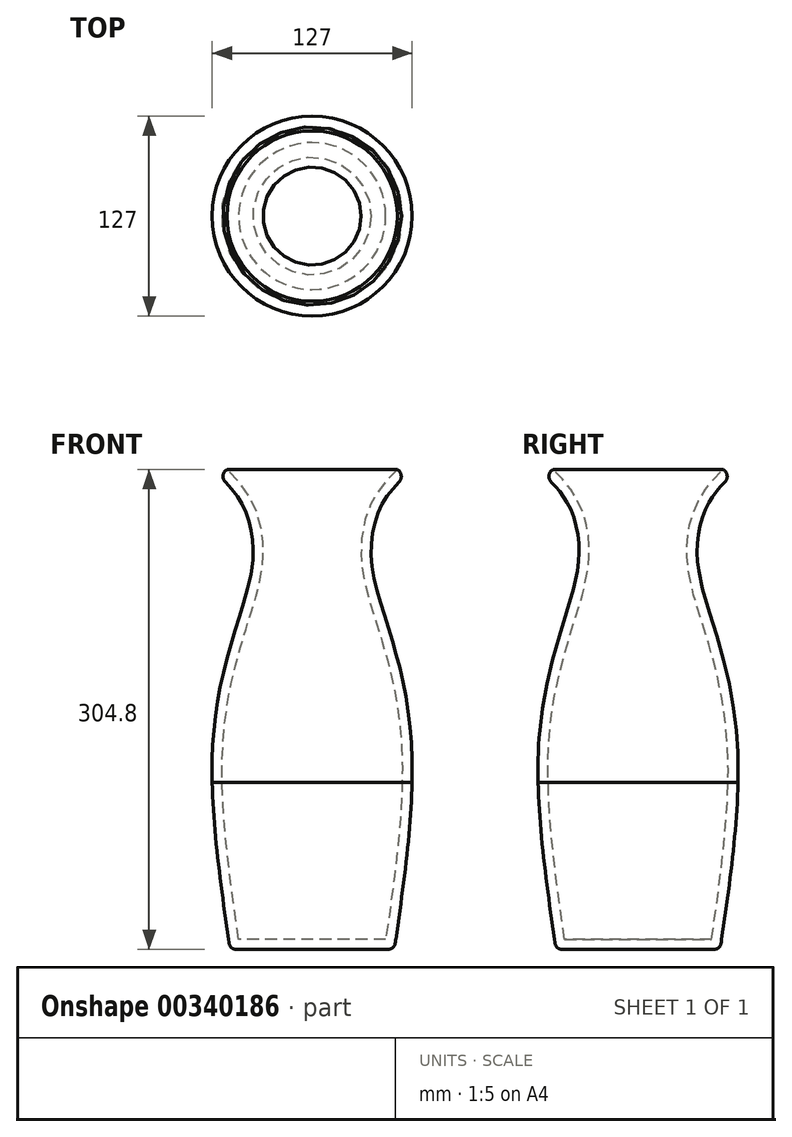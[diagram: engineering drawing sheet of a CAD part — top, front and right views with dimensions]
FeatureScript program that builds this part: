
annotation { "Feature Type Name" : "Feature", "Feature Type Description" : "" }
export const myFeature = defineFeature(function(context is Context, id is Id, definition is map)
    precondition{}
    {
        {
            var Q0;
            Q0=qCreatedBy(makeId("Front.planeOp"),FACE);
            var sketch = newSketch(context, id + "F0", { "sketchPlane" : qUnion([Q0])});
            skLineSegment(sketch, "E0.bottom", {"start": v(31.75, 152.4) * mm, "end": v(-31.75, 152.4) * mm});
            skLineSegment(sketch, "E0.top", {"start": v(31.75, -152.4) * mm, "end": v(-31.75, -152.4) * mm});
            skLineSegment(sketch, "E0.left", {"start": v(31.75, 152.4) * mm, "end": v(31.75, -152.4) * mm});
            skLineSegment(sketch, "E0.right", {"start": v(-31.75, 152.4) * mm, "end": v(-31.75, -152.4) * mm});
            skPoint(sketch, "E0.middle", {"position": v(0, 0) * mm});
            skFitSpline(sketch, "E1", {"points": [v(-31.75, 152.4) * mm, v(-13.17, 131.2) * mm, v(-5.9, 95.37) * mm, v(-19.4, 42.9) * mm, v(-31.75, -31.89) * mm, v(-20.44, -152.4) * mm], "startDerivative": vector(149.57, -137.06) * mm, "endDerivative": vector(63.8, -443.79) * mm});
            skFitSpline(sketch, "E2.0", {"points": [v(-27.46, 157.08) * mm, v(-25.9, 155.65) * mm, v(-22.73, 152.75) * mm, v(-17.97, 148.09) * mm, v(-14.14, 143.8) * mm, v(-11.26, 140.04) * mm, v(-9.55, 137.54) * mm, v(-8.26, 135.43) * mm, v(-7.02, 133.26) * mm, v(-5.6, 130.44) * mm, v(-4.09, 126.9) * mm, v(-2.34, 121.98) * mm, v(-0.66, 115.53) * mm, v(0.31, 108.73) * mm, v(0.64, 103.13) * mm, v(0.66, 99.58) * mm, v(0.56, 96.7) * mm, v(0.37, 93.82) * mm, v(0, 90.2) * mm, v(-0.66, 85.88) * mm, v(-1.78, 80.1) * mm, v(-3.55, 72.87) * mm, v(-6.1, 64.13) * mm, v(-8.88, 55.32) * mm, v(-11.25, 47.89) * mm, v(-13.09, 41.89) * mm, v(-14.87, 35.84) * mm, v(-16.96, 28.14) * mm, v(-19.23, 18.65) * mm, v(-21.22, 8.87) * mm, v(-22.89, -1.23) * mm, v(-24.19, -11.68) * mm, v(-24.93, -20.73) * mm, v(-25.3, -28.18) * mm, v(-25.51, -35.78) * mm, v(-25.48, -45.6) * mm, v(-25.01, -57.84) * mm, v(-24.17, -70.48) * mm, v(-23, -83.45) * mm, v(-21.08, -101.12) * mm, v(-18.14, -123.79) * mm, v(-15.48, -142.25) * mm, v(-14.15, -151.5) * mm]});
            skLineSegment(sketch, "E3.0", {"start": v(31.75, -146.05) * mm, "end": v(-31.75, -146.05) * mm});
            skSolve(sketch);
        }
        {
            var Q0;
            {var subQ0=sQuery(id+"F0.wireOp",EDGE,"E1");var subQ1=sQuery(id+"F0.wireOp",EDGE,"E0.right");var subQ4=makeQuery(id+"F0.imprint","INTERSECT",VERTEX,{"disambiguationData":[OD(0.0)],"derivedFrom":[subQ1,subQ0]});Q0=makeQuery(id+"F0.imprint","IMPRINT",FACE,{"disambiguationData":[TD([[makeQuery(id+"F0.imprint","IMPRINT",EDGE,{"disambiguationData":[TD([[subQ4,-1.0]])],"derivedFrom":subQ1}),1.0]])]});}
            var Q1;
            {var subQ1=sQuery(id+"F0.wireOp",EDGE,"E0.top");var subQ5=sQuery(id+"F0.wireOp",EDGE,"E0.left");var subQ6=makeQuery(id+"F0.imprint","INTERSECT",VERTEX,{"derivedFrom":[subQ1,subQ5]});Q1=makeQuery(id+"F0.imprint","IMPRINT",FACE,{"disambiguationData":[TD([[makeQuery(id+"F0.imprint","IMPRINT",EDGE,{"disambiguationData":[TD([[subQ6,-1.0]])],"derivedFrom":subQ1}),-1.0]])]});}
            var Q2;
            Q2=sQuery(id+"F0.wireOp",EDGE,"E0.left");
            revolve(context, id + "F1", {"entities" : qUnion([Q0, Q1]), "axis" : qUnion([Q2]), "revolveType" : RevolveType.FULL});
        }
        {
            var Q0;
            {var subQ0=sQuery(id+"F0.wireOp",EDGE,"E1");var subQ1=sQuery(id+"F0.wireOp",EDGE,"E0.right");Q0=makeQuery(id+"F1.opRevolve","SWEPT_FACE",FACE,{"disambiguationData":[OSD([subQ0]),TDD([makeQuery(id+"F0.imprint","IMPRINT",EDGE,{"disambiguationData":[TD([[makeQuery(id+"F0.imprint","INTERSECT",VERTEX,{"disambiguationData":[OD(0.0)],"derivedFrom":[subQ1,subQ0]}),1.0]])],"derivedFrom":subQ0})])]});}
            fillet(context, id + "F2", {"entities" : qUnion([Q0]), "radius" : 5.08 * mm, "tangentPropagation" : true, "allowEdgeOverflow" : false});
        }
        {
            var Q0;
            Q0=makeQuery(id+"F1.opRevolve","SWEPT_EDGE",EDGE,{"disambiguationData":[OSD([sQuery(id+"F0.wireOp",EDGE,"E0.top"),sQuery(id+"F0.wireOp",EDGE,"E1")])]});
            fillet(context, id + "F3", {"entities" : qUnion([Q0]), "radius" : 5.08 * mm, "tangentPropagation" : true, "rho" : 0.5, "crossSection" : FilletCrossSection.CONIC, "allowEdgeOverflow" : false});
        }
    });
